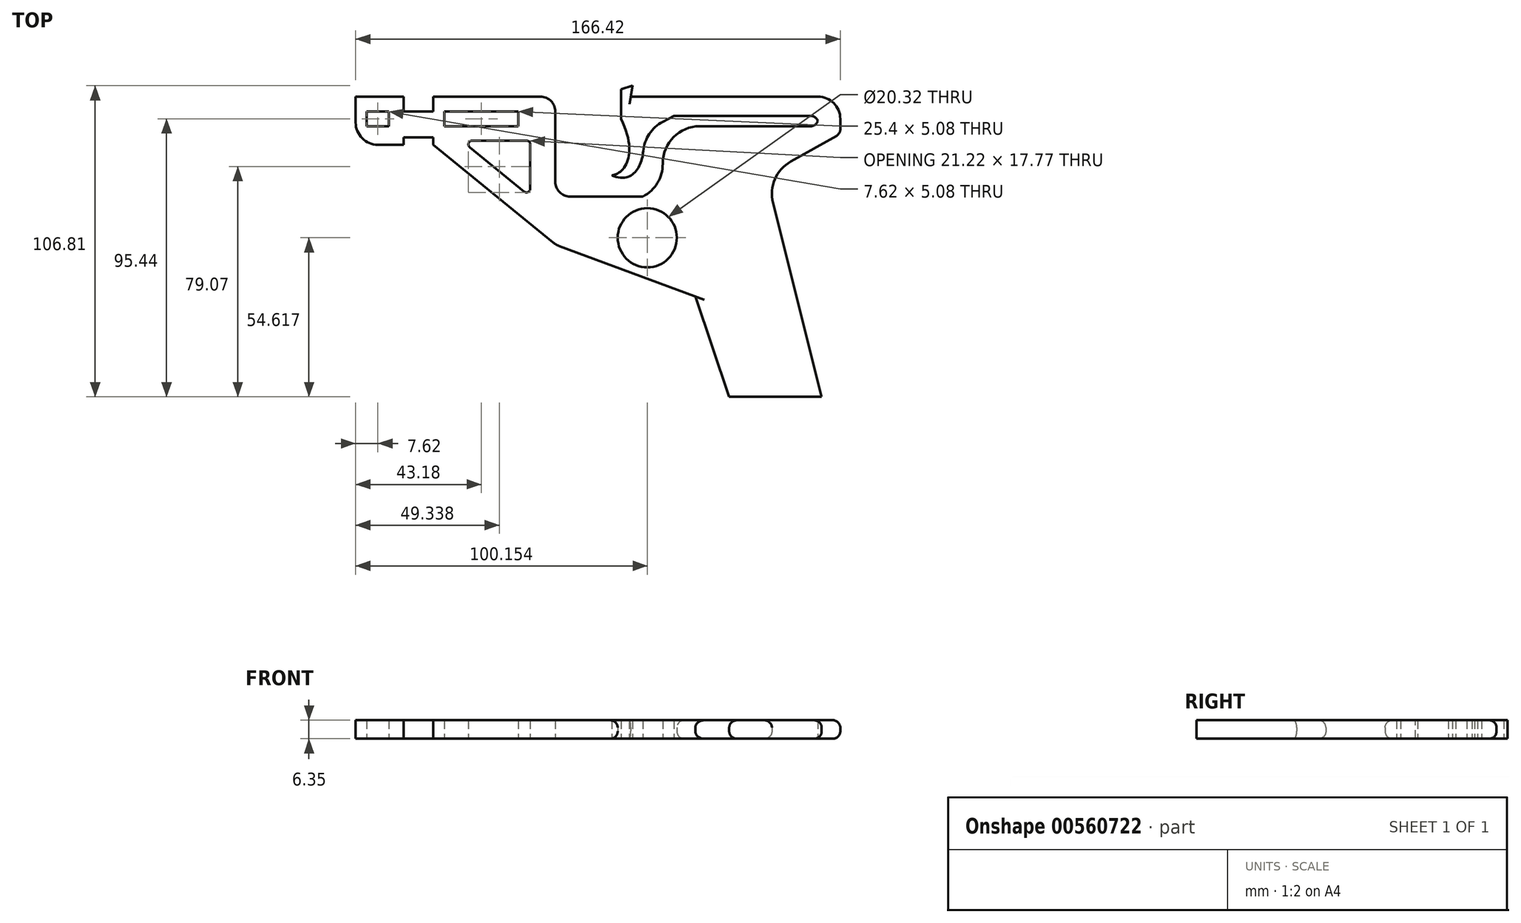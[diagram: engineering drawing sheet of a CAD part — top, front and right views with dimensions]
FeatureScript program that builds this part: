
annotation { "Feature Type Name" : "Feature", "Feature Type Description" : "" }
export const myFeature = defineFeature(function(context is Context, id is Id, definition is map)
    precondition{}
    {
        {
            var Q0;
            Q0=qCreatedBy(makeId("Top.planeOp"),FACE);
            var sketch = newSketch(context, id + "F0", { "sketchPlane" : qUnion([Q0])});
            skLineSegment(sketch, "E0", {"start": v(15.3, -6.59) * mm, "end": v(-31.67, -6.59) * mm});
            skLineSegment(sketch, "E1", {"start": v(-49.82, 0) * mm, "end": v(-49.82, 2.54) * mm});
            skLineSegment(sketch, "E2", {"start": v(-49.82, 2.54) * mm, "end": v(-45.83, 3.75) * mm});
            skLineSegment(sketch, "E3", {"start": v(-45.83, 3.75) * mm, "end": v(-46.49, 0) * mm});
            skLineSegment(sketch, "E4", {"start": v(-49.82, 0) * mm, "end": v(-49.82, -7.6) * mm});
            skFitSpline(sketch, "E5", {"points": [v(-49.82, -7.6) * mm, v(-52.97, -27.04) * mm], "startDerivative": vector(17.78, -36.67) * mm, "endDerivative": vector(-13.9, -2.22) * mm});
            skPoint(sketch, "E6.end.orphan", {"position": v(4.63, 0) * mm});
            skPoint(sketch, "E6.start.orphan", {"position": v(0, 0) * mm});
            skLineSegment(sketch, "E7", {"start": v(-46.49, 0) * mm, "end": v(12.04, 0) * mm});
            skLineSegment(sketch, "E8", {"start": v(-31.67, -6.59) * mm, "end": v(-35.5, -8.63) * mm});
            skFitSpline(sketch, "E9", {"points": [v(-43.15, -12.7) * mm, v(-52.97, -27.04) * mm], "startDerivative": vector(8.33, -14.45) * mm, "endDerivative": vector(-29.45, 12.78) * mm});
            skArc(sketch, "E10.filletArc", {"start": v(-51.6, -26.65) * mm, "mid": v(-51.9, -27.12) * mm, "end": v(-51.54, -27.55) * mm});
            skLineSegment(sketch, "E11", {"start": v(17.83, -7.62) * mm, "end": v(17.83, -9.13) * mm});
            skLineSegment(sketch, "E12", {"start": v(15.3, -10.16) * mm, "end": v(-22.8, -10.16) * mm});
            skLineSegment(sketch, "E13", {"start": v(-35.5, -22.86) * mm, "end": v(-35.5, -23.07) * mm});
            skLineSegment(sketch, "E14", {"start": v(-24.33, -68.61) * mm, "end": v(-12.7, -103.06) * mm});
            skLineSegment(sketch, "E15", {"start": v(-12.7, -103.06) * mm, "end": v(19.05, -103.06) * mm});
            skLineSegment(sketch, "E16", {"start": v(19.05, -103.06) * mm, "end": v(2.35, -36.44) * mm});
            skLineSegment(sketch, "E17", {"start": v(8.44, -22.29) * mm, "end": v(24.16, -13.43) * mm});
            skLineSegment(sketch, "E18", {"start": v(25.45, -11.22) * mm, "end": v(25.45, -7.62) * mm});
            skLineSegment(sketch, "E19", {"start": v(17.83, 0) * mm, "end": v(12.04, 0) * mm});
            skPoint(sketch, "E20.visualSharp", {"position": v(-35.5, -10.16) * mm});
            skArc(sketch, "E20.filletArc", {"start": v(-22.8, -10.16) * mm, "mid": v(-31.79, -13.88) * mm, "end": v(-35.5, -22.86) * mm});
            skPoint(sketch, "E21.visualSharp", {"position": v(-33.64, -41.03) * mm});
            skPoint(sketch, "E22.visualSharp", {"position": v(0, -27.04) * mm});
            skArc(sketch, "E22.filletArc", {"start": v(8.44, -22.29) * mm, "mid": v(3, -28.33) * mm, "end": v(2.35, -36.44) * mm});
            skArc(sketch, "E23.filletArc", {"start": v(-35.5, -8.63) * mm, "mid": v(-40.13, -12.83) * mm, "end": v(-42.2, -18.72) * mm});
            skPoint(sketch, "E24.visualSharp", {"position": v(-35.5, -32.54) * mm});
            skArc(sketch, "E24.filletArc", {"start": v(-42.26, -34.3) * mm, "mid": v(-37.33, -29.62) * mm, "end": v(-35.5, -23.07) * mm});
            skLineSegment(sketch, "E25", {"start": v(-77.47, 0) * mm, "end": v(-114.3, 0) * mm});
            skLineSegment(sketch, "E26", {"start": v(-124.46, 0) * mm, "end": v(-140.97, 0) * mm});
            skLineSegment(sketch, "E27", {"start": v(-140.97, 0) * mm, "end": v(-140.97, -8.9) * mm});
            skLineSegment(sketch, "E28", {"start": v(-133.35, -16.51) * mm, "end": v(-124.46, -16.51) * mm});
            skLineSegment(sketch, "E29", {"start": v(-124.46, -16.51) * mm, "end": v(-124.46, -13.97) * mm});
            skLineSegment(sketch, "E30", {"start": v(-124.46, -13.97) * mm, "end": v(-114.3, -13.97) * mm});
            skLineSegment(sketch, "E31", {"start": v(-114.3, -13.97) * mm, "end": v(-114.3, -16.51) * mm});
            skLineSegment(sketch, "E32", {"start": v(-71.03, -51.29) * mm, "end": v(-24.33, -68.61) * mm});
            skLineSegment(sketch, "E33", {"start": v(-72.4, -5.08) * mm, "end": v(-72.4, -29.21) * mm});
            skPoint(sketch, "E34.orphan", {"position": v(-54.47, 0) * mm});
            skLineSegment(sketch, "E35", {"start": v(-73.2, -50.05) * mm, "end": v(-114.3, -16.51) * mm});
            skLineSegment(sketch, "E36", {"start": v(-42.26, -34.3) * mm, "end": v(-67.31, -34.3) * mm});
            skPoint(sketch, "E37.orphan", {"position": v(-72.4, -30.85) * mm});
            skPoint(sketch, "E38.visualSharp", {"position": v(17.83, -10.16) * mm});
            skArc(sketch, "E38.filletArc", {"start": v(15.3, -10.16) * mm, "mid": v(17.09, -9.42) * mm, "end": v(17.83, -7.62) * mm});
            skPoint(sketch, "E39.visualSharp", {"position": v(-72.4, -34.3) * mm});
            skArc(sketch, "E39.filletArc", {"start": v(-72.4, -29.21) * mm, "mid": v(-70.9, -32.8) * mm, "end": v(-67.31, -34.3) * mm});
            skPoint(sketch, "E40.visualSharp", {"position": v(-72.4, 0) * mm});
            skArc(sketch, "E40.filletArc", {"start": v(-72.39, -5.08) * mm, "mid": v(-73.88, -1.49) * mm, "end": v(-77.47, 0) * mm});
            skPoint(sketch, "E41.end.orphan", {"position": v(-118.3, -10.16) * mm});
            skPoint(sketch, "E42.start.orphan", {"position": v(-124.46, -10.16) * mm});
            skLineSegment(sketch, "E43", {"start": v(-124.46, 0) * mm, "end": v(-124.46, -5.08) * mm});
            skLineSegment(sketch, "E44", {"start": v(-124.46, -5.08) * mm, "end": v(-114.3, -5.08) * mm});
            skLineSegment(sketch, "E45", {"start": v(-114.3, -5.08) * mm, "end": v(-114.3, 0) * mm});
            skPoint(sketch, "E46.visualSharp", {"position": v(-140.97, -16.51) * mm});
            skArc(sketch, "E46.filletArc", {"start": v(-140.97, -8.9) * mm, "mid": v(-138.74, -14.28) * mm, "end": v(-133.35, -16.51) * mm});
            skPoint(sketch, "E47.visualSharp", {"position": v(-72.22, -50.85) * mm});
            skArc(sketch, "E47.filletArc", {"start": v(-73.2, -50.05) * mm, "mid": v(-72.16, -50.76) * mm, "end": v(-71.03, -51.29) * mm});
            skPoint(sketch, "E48.visualSharp", {"position": v(25.45, 0) * mm});
            skArc(sketch, "E48.filletArc", {"start": v(25.45, -7.62) * mm, "mid": v(23.22, -2.23) * mm, "end": v(17.83, 0) * mm});
            skPoint(sketch, "E49.visualSharp", {"position": v(17.83, -6.59) * mm});
            skArc(sketch, "E49.filletArc", {"start": v(17.83, -9.13) * mm, "mid": v(17.09, -7.33) * mm, "end": v(15.3, -6.59) * mm});
            skPoint(sketch, "E50.visualSharp", {"position": v(25.45, -12.7) * mm});
            skArc(sketch, "E50.filletArc", {"start": v(24.16, -13.43) * mm, "mid": v(25.1, -12.5) * mm, "end": v(25.45, -11.22) * mm});
            skLineSegment(sketch, "E51.bottom", {"start": v(-110.5, -5.08) * mm, "end": v(-85.1, -5.08) * mm});
            skLineSegment(sketch, "E51.top", {"start": v(-110.5, -10.16) * mm, "end": v(-85.1, -10.16) * mm});
            skLineSegment(sketch, "E51.left", {"start": v(-110.5, -5.08) * mm, "end": v(-110.5, -10.16) * mm});
            skLineSegment(sketch, "E51.right", {"start": v(-85.1, -5.08) * mm, "end": v(-85.1, -10.16) * mm});
            skLineSegment(sketch, "E52.bottom", {"start": v(-129.54, -5.08) * mm, "end": v(-137.16, -5.08) * mm});
            skLineSegment(sketch, "E52.top", {"start": v(-129.54, -10.16) * mm, "end": v(-137.16, -10.16) * mm});
            skLineSegment(sketch, "E52.left", {"start": v(-129.54, -5.08) * mm, "end": v(-129.54, -10.16) * mm});
            skLineSegment(sketch, "E52.right", {"start": v(-137.16, -5.08) * mm, "end": v(-137.16, -10.16) * mm});
            skCircle(sketch, "E53", {"center": v(-40.82, -48.44) * mm, "radius": 10.16 * mm});
            skLineSegment(sketch, "E54", {"start": v(-101.77, -17.36) * mm, "end": v(-83.1, -32.6) * mm});
            skLineSegment(sketch, "E55", {"start": v(-81.02, -31.61) * mm, "end": v(-81.02, -16.37) * mm});
            skLineSegment(sketch, "E56", {"start": v(-82.3, -15.1) * mm, "end": v(-100.97, -15.1) * mm});
            skPoint(sketch, "E57.visualSharp", {"position": v(-104.54, -15.1) * mm});
            skArc(sketch, "E57.filletArc", {"start": v(-100.97, -15.1) * mm, "mid": v(-102.17, -15.95) * mm, "end": v(-101.77, -17.36) * mm});
            skPoint(sketch, "E58.visualSharp", {"position": v(-81.02, -15.1) * mm});
            skArc(sketch, "E58.filletArc", {"start": v(-81.02, -16.37) * mm, "mid": v(-81.4, -15.48) * mm, "end": v(-82.3, -15.1) * mm});
            skPoint(sketch, "E59.visualSharp", {"position": v(-81.02, -34.3) * mm});
            skArc(sketch, "E59.filletArc", {"start": v(-83.1, -32.6) * mm, "mid": v(-81.75, -32.76) * mm, "end": v(-81.02, -31.61) * mm});
            skPoint(sketch, "E60.endSnap0", {"position": v(-23.76, -47.57) * mm});
            skPoint(sketch, "E61.endSnap0", {"position": v(-1.83, -60.66) * mm});
            skPoint(sketch, "E62.orphan", {"position": v(-1.83, -59.15) * mm});
            skPoint(sketch, "E63.trimOffspring.end.orphan", {"position": v(-28.7, -36.95) * mm});
            skPoint(sketch, "E64.start.orphan", {"position": v(-10.75, -25.04) * mm});
            skPoint(sketch, "E65.orphan", {"position": v(-18.81, -58.2) * mm});
            skPoint(sketch, "E66.start.orphan", {"position": v(-23.76, -45.73) * mm});
            skPoint(sketch, "E67.trimOffspring.end.orphan", {"position": v(7.1, -96.28) * mm});
            skSolve(sketch);
        }
        {
            var Q0;
            Q0 = qSketchRegion(id + "F0", true);
            extrude(context, id + "F1", {"entities" : qUnion([Q0]), "depth" : 6.35 * mm, "offsetDistance" : 25.4 * mm});
        }
        {
            var Q0;
            Q0=makeQuery(id+"F1.opExtrude","CAP_EDGE",EDGE,{"disambiguationData":[OSD([sQuery(id+"F0.wireOp",EDGE,"E14")])],"isStart":false});
            var Q1;
            Q1=makeQuery(id+"F1.opExtrude","CAP_EDGE",EDGE,{"disambiguationData":[OSD([sQuery(id+"F0.wireOp",EDGE,"E14")])],"isStart":true});
            var Q2;
            Q2=makeQuery(id+"F1.opExtrude","CAP_EDGE",EDGE,{"disambiguationData":[OSD([sQuery(id+"F0.wireOp",EDGE,"E53")])],"isStart":false});
            var Q3;
            Q3=makeQuery(id+"F1.opExtrude","CAP_EDGE",EDGE,{"disambiguationData":[OSD([sQuery(id+"F0.wireOp",EDGE,"E53")])],"isStart":true});
            var Q4;
            Q4=makeQuery(id+"F1.opExtrude","CAP_EDGE",EDGE,{"disambiguationData":[OSD([sQuery(id+"F0.wireOp",EDGE,"E16")])],"isStart":false});
            var Q5;
            Q5=makeQuery(id+"F1.opExtrude","CAP_EDGE",EDGE,{"disambiguationData":[OSD([sQuery(id+"F0.wireOp",EDGE,"E16")])],"isStart":true});
            fillet(context, id + "F2", {"entities" : qUnion([Q0, Q1, Q2, Q3, Q4, Q5]), "radius" : 2.54 * mm, "tangentPropagation" : true, "allowEdgeOverflow" : false});
        }
    });
